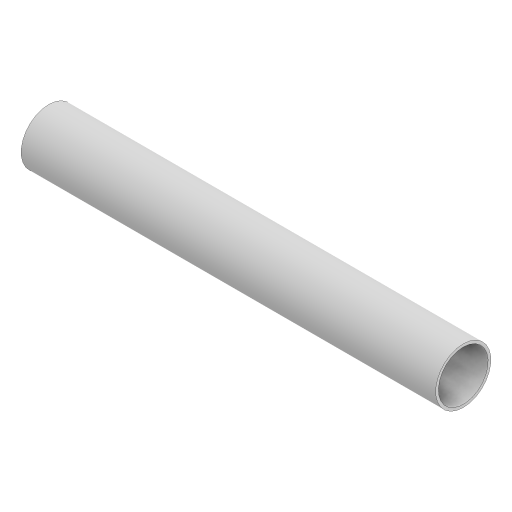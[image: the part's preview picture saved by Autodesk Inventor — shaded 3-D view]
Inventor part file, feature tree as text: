
AUTODESK INVENTOR PART (.ipt)
format: ipt  version: 2024.3 (Build 283343000, 343)  size: 93,184 bytes
history: native  units: mm
features: extrude x1, sketch x1
ambient origin geometry x8: Origin, YZ Plane, XZ Plane, XY Plane, X Axis, Y Axis, Z Axis, Center Point
bodies: Solid1 (feature_tree)
feature tree (2):
  extrude  "Extrusion1"  Depth=150.0mm
  sketch  "Sketch1"  dims[d0=20.0mm d1=1.0mm d2=150.0mm d3=0.0mm]
